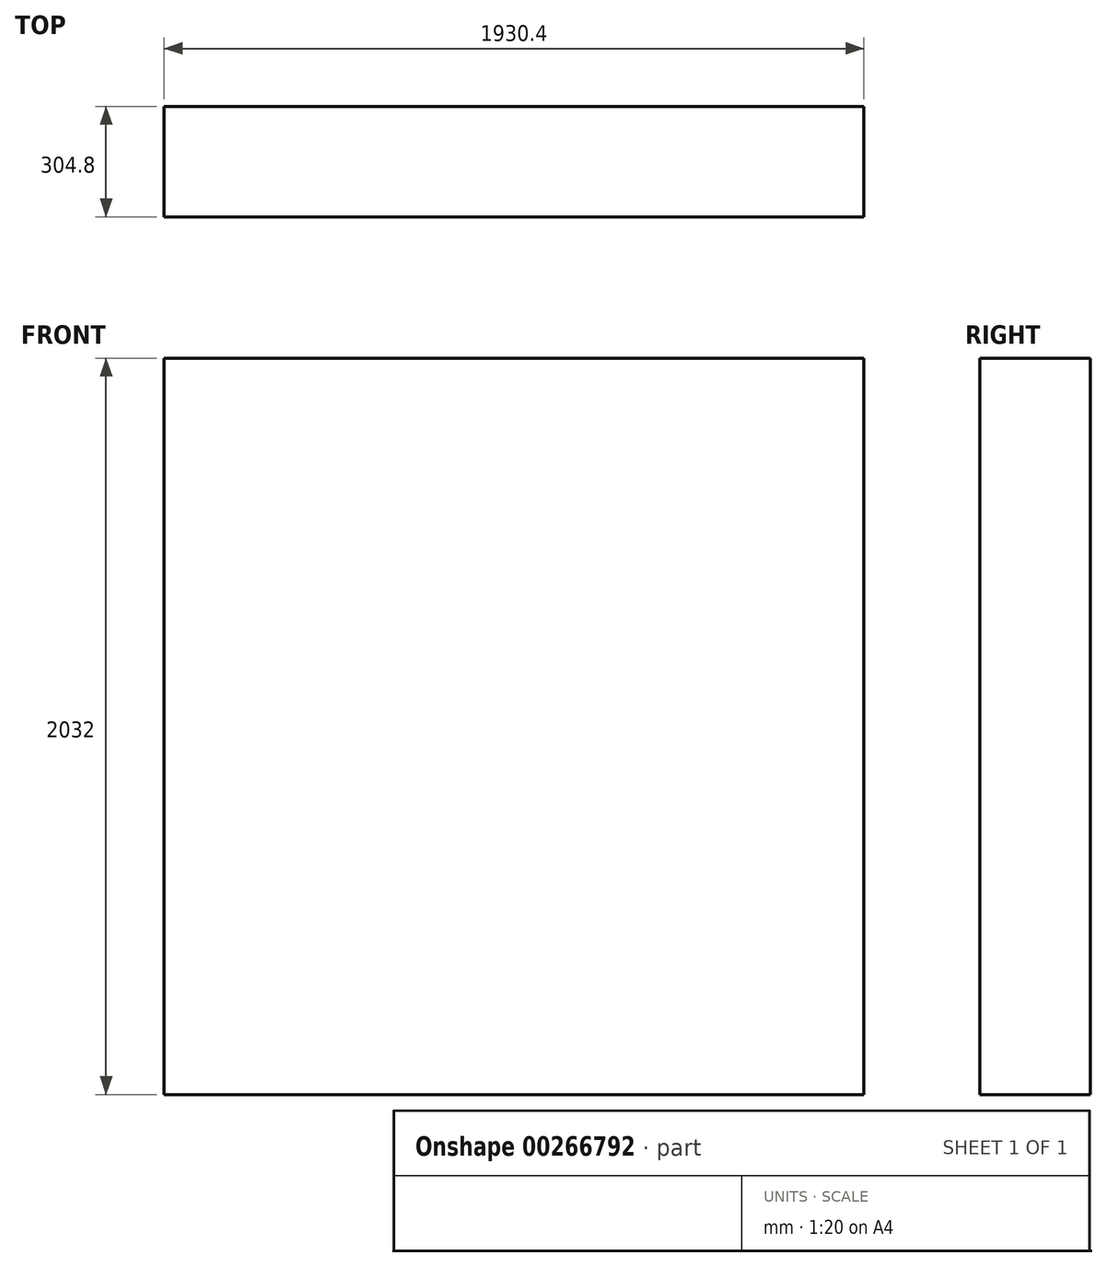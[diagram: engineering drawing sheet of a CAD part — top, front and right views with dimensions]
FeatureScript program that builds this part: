
annotation { "Feature Type Name" : "Feature", "Feature Type Description" : "" }
export const myFeature = defineFeature(function(context is Context, id is Id, definition is map)
    precondition{}
    {
        {
            var Q0;
            Q0=qCreatedBy(makeId("Front.planeOp"),FACE);
            var sketch = newSketch(context, id + "F0", { "sketchPlane" : qUnion([Q0])});
            skLineSegment(sketch, "E0.bottom", {"start": v(-48.34, 2017.58) * mm, "end": v(1882.06, 2017.58) * mm});
            skLineSegment(sketch, "E0.top", {"start": v(-48.34, -14.42) * mm, "end": v(1882.06, -14.42) * mm});
            skLineSegment(sketch, "E0.left", {"start": v(-48.34, 2017.58) * mm, "end": v(-48.34, -14.42) * mm});
            skLineSegment(sketch, "E0.right", {"start": v(1882.06, 2017.58) * mm, "end": v(1882.06, -14.42) * mm});
            skSolve(sketch);
        }
        {
            var Q0;
            Q0=qSketchRegion(id+"F0",true);
            extrude(context, id + "F1", {"entities" : qUnion([Q0]), "depth" : 304.8 * mm});
        }
    });
